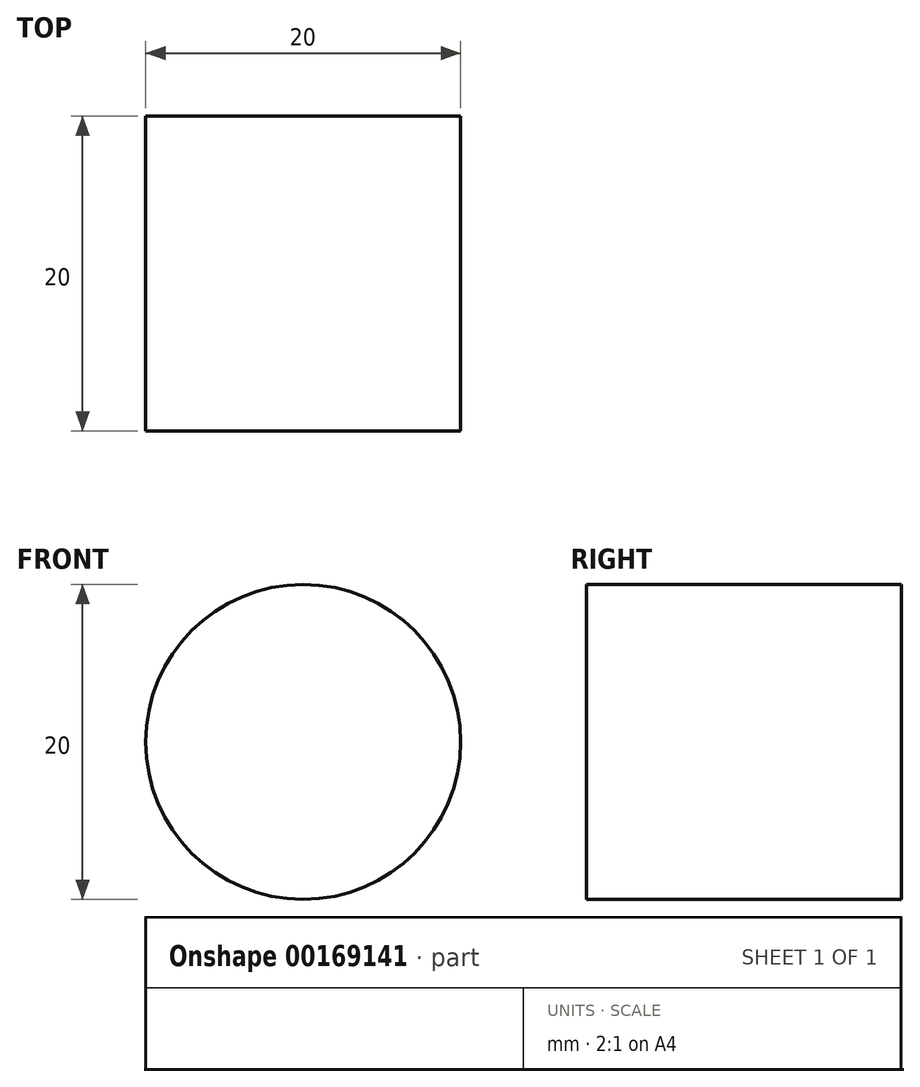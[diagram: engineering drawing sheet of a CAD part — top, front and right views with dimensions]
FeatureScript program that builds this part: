
annotation { "Feature Type Name" : "Feature", "Feature Type Description" : "" }
export const myFeature = defineFeature(function(context is Context, id is Id, definition is map)
    precondition{}
    {
        {
            var Q0;
            Q0=qCreatedBy(makeId("Front.planeOp"),FACE);
            var sketch = newSketch(context, id + "F0", { "sketchPlane" : qUnion([Q0])});
            skCircle(sketch, "E0", {"center": v(0, 0) * mm, "radius": 10 * mm});
            skSolve(sketch);
        }
        {
            var Q0;
            Q0=makeQuery(id+"F0.imprint","IMPRINT",FACE,{"disambiguationData":[TD([[makeQuery(id+"F0.imprint","IMPRINT",EDGE,{"derivedFrom":sQuery(id+"F0.wireOp",EDGE,"E0")}),1.0]])]});
            extrude(context, id + "F1", {"entities" : qUnion([Q0]), "depth" : 20 * mm});
        }
    });
